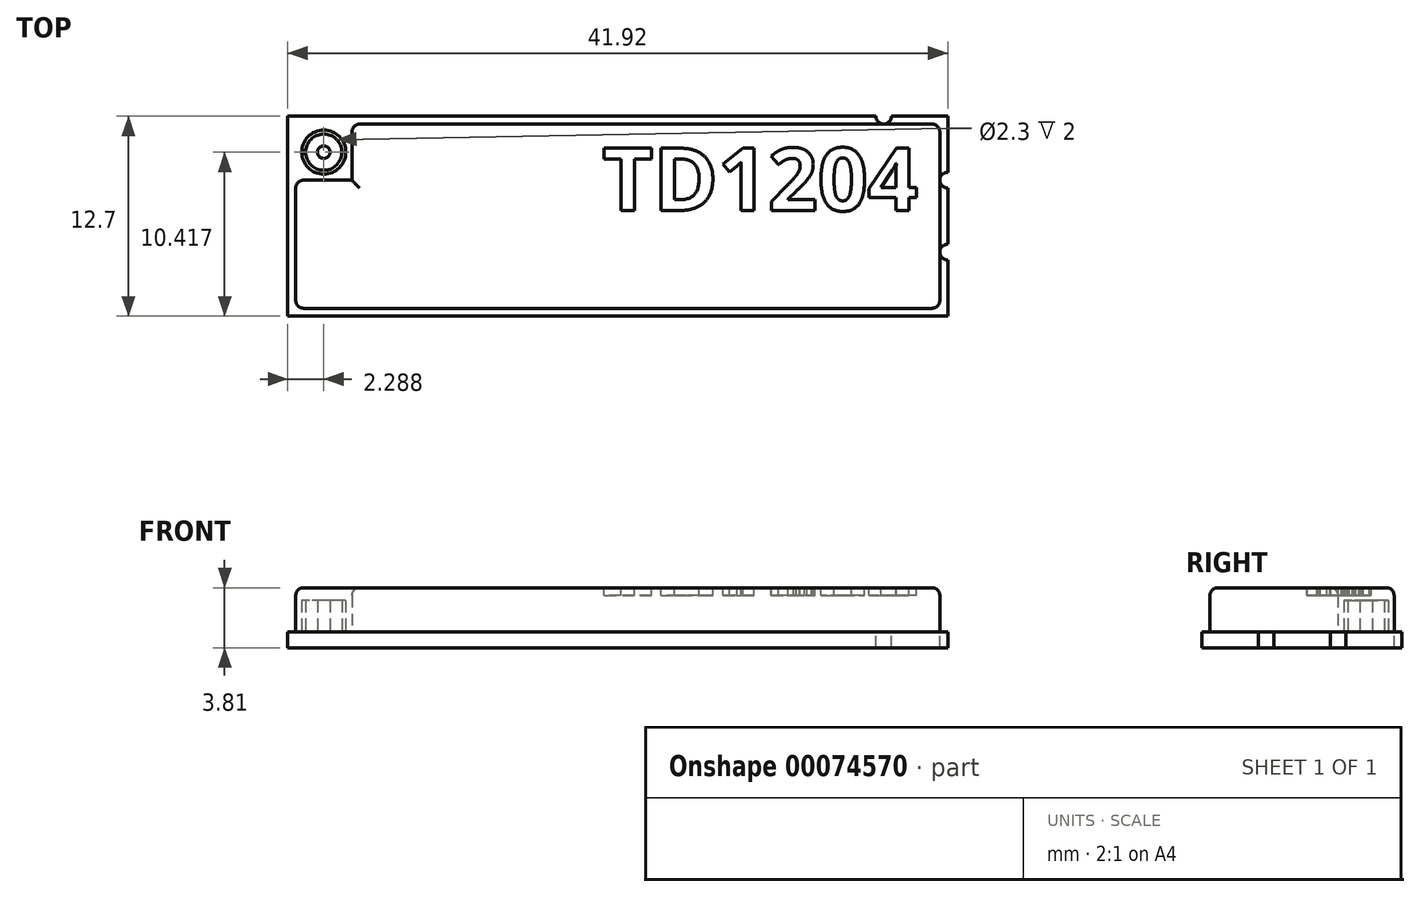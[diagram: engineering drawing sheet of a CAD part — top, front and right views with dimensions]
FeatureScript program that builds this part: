
annotation { "Feature Type Name" : "Feature", "Feature Type Description" : "" }
export const myFeature = defineFeature(function(context is Context, id is Id, definition is map)
    precondition{}
    {
        {
            var Q0;
            Q0=qCreatedBy(makeId("Top.planeOp"),FACE);
            var sketch = newSketch(context, id + "F0", { "sketchPlane" : qUnion([Q0])});
            skLineSegment(sketch, "E0.rect.bottom", {"start": v(-20.95, -6.35) * mm, "end": v(20.95, -6.35) * mm});
            skLineSegment(sketch, "E0.rect.top", {"start": v(-20.95, 6.35) * mm, "end": v(16.39, 6.35) * mm});
            skLineSegment(sketch, "E0.rect.left", {"start": v(-20.95, -6.35) * mm, "end": v(-20.95, 6.35) * mm});
            skLineSegment(sketch, "E0.rect.right", {"start": v(20.95, -6.35) * mm, "end": v(20.95, -2.78) * mm});
            skPoint(sketch, "E0.rect.middle", {"position": v(0, 0) * mm});
            skLineSegment(sketch, "E1.0", {"start": v(-16.89, 5.85) * mm, "end": v(20.45, 5.85) * mm});
            skLineSegment(sketch, "E1.1", {"start": v(-20.45, -5.85) * mm, "end": v(-20.45, 2.28) * mm});
            skLineSegment(sketch, "E1.2", {"start": v(-20.45, -5.85) * mm, "end": v(20.45, -5.85) * mm});
            skLineSegment(sketch, "E1.3", {"start": v(20.45, -5.85) * mm, "end": v(20.45, 5.85) * mm});
            skArc(sketch, "E2", {"start": v(20.95, 2.78) * mm, "mid": v(20.45, 2.28) * mm, "end": v(20.95, 1.78) * mm});
            skArc(sketch, "E3", {"start": v(20.95, -1.78) * mm, "mid": v(20.45, -2.28) * mm, "end": v(20.95, -2.78) * mm});
            skLineSegment(sketch, "E4.trimOffspring", {"start": v(20.95, 2.78) * mm, "end": v(20.95, 6.35) * mm});
            skLineSegment(sketch, "E5.trimOffspring", {"start": v(20.95, -1.78) * mm, "end": v(20.95, 1.78) * mm});
            skLineSegment(sketch, "E6", {"start": v(20.45, 5.85) * mm, "end": v(20.95, 6.35) * mm, "construction": true});
            skArc(sketch, "E7.MirrorCS", {"start": v(17.39, 6.35) * mm, "mid": v(16.89, 5.85) * mm, "end": v(16.39, 6.35) * mm});
            skLineSegment(sketch, "E8.trimOffspring", {"start": v(17.39, 6.35) * mm, "end": v(20.95, 6.35) * mm});
            skLineSegment(sketch, "E9", {"start": v(-20.45, 2.28) * mm, "end": v(-16.89, 2.28) * mm});
            skLineSegment(sketch, "E10", {"start": v(-16.89, 2.28) * mm, "end": v(-16.89, 5.85) * mm});
            skLineSegment(sketch, "E11", {"start": v(-20.45, 2.28) * mm, "end": v(-16.89, 5.85) * mm, "construction": true});
            skCircle(sketch, "E12", {"center": v(-18.67, 4.07) * mm, "radius": 1.4 * mm});
            skCircle(sketch, "E13", {"center": v(-18.67, 4.07) * mm, "radius": 1.15 * mm});
            skCircle(sketch, "E14", {"center": v(-18.67, 4.07) * mm, "radius": 0.4 * mm});
            skSolve(sketch);
        }
        {
            var Q0;
            Q0=makeQuery(id+"F0.imprint","IMPRINT",FACE,{"disambiguationData":[TD([[makeQuery(id+"F0.imprint","IMPRINT",EDGE,{"derivedFrom":sQuery(id+"F0.wireOp",EDGE,"E1.1")}),-1.0]])]});
            extrude(context, id + "F1", {"entities" : qUnion([Q0]), "depth" : (3.81 - 1) * mm});
        }
        {
            var Q0;
            Q0=makeQuery(id+"F0.imprint","IMPRINT",FACE,{"disambiguationData":[TD([[makeQuery(id+"F0.imprint","IMPRINT",EDGE,{"derivedFrom":sQuery(id+"F0.wireOp",EDGE,"E0.rect.bottom")}),1.0]])]});
            var Q1;
            Q1=makeQuery(id+"F0.imprint","IMPRINT",FACE,{"disambiguationData":[TD([[makeQuery(id+"F0.imprint","IMPRINT",EDGE,{"derivedFrom":sQuery(id+"F0.wireOp",EDGE,"E12")}),1.0]])]});
            var Q2;
            Q2=makeQuery(id+"F0.imprint","IMPRINT",FACE,{"disambiguationData":[TD([[makeQuery(id+"F0.imprint","IMPRINT",EDGE,{"derivedFrom":sQuery(id+"F0.wireOp",EDGE,"E13")}),1.0]])]});
            var Q3;
            {var subQ5=sQuery(id+"F0.wireOp",EDGE,"E5.trimOffspring");Q3=makeQuery(id+"F0.imprint","IMPRINT",FACE,{"disambiguationData":[TD([[makeQuery(id+"F0.imprint","IMPRINT",EDGE,{"derivedFrom":subQ5}),1.0]])]});}
            var Q4;
            {var subQ0=sQuery(id+"F0.wireOp",EDGE,"E4.trimOffspring");Q4=makeQuery(id+"F0.imprint","IMPRINT",FACE,{"disambiguationData":[TD([[makeQuery(id+"F0.imprint","IMPRINT",EDGE,{"derivedFrom":subQ0}),1.0]])]});}
            var Q5;
            Q5=makeQuery(id+"F0.imprint","IMPRINT",FACE,{"disambiguationData":[TD([[makeQuery(id+"F0.imprint","IMPRINT",EDGE,{"derivedFrom":sQuery(id+"F0.wireOp",EDGE,"E1.1")}),-1.0]])]});
            var Q6;
            Q6=makeQuery(id+"F0.imprint","IMPRINT",FACE,{"disambiguationData":[TD([[makeQuery(id+"F0.imprint","IMPRINT",EDGE,{"derivedFrom":sQuery(id+"F0.wireOp",EDGE,"E14")}),1.0]])]});
            extrude(context, id + "F2", {"entities" : qUnion([Q0, Q1, Q2, Q3, Q4, Q5, Q6]), "operationType" : NewBodyOperationType.ADD, "oppositeDirection" : true, "depth" : 1 * mm});
        }
        {
            var Q0;
            Q0=makeQuery(id+"F0.imprint","IMPRINT",FACE,{"disambiguationData":[TD([[makeQuery(id+"F0.imprint","IMPRINT",EDGE,{"derivedFrom":sQuery(id+"F0.wireOp",EDGE,"E12")}),1.0]])]});
            var Q1;
            Q1=makeQuery(id+"F0.imprint","IMPRINT",FACE,{"disambiguationData":[TD([[makeQuery(id+"F0.imprint","IMPRINT",EDGE,{"derivedFrom":sQuery(id+"F0.wireOp",EDGE,"E14")}),1.0]])]});
            extrude(context, id + "F3", {"entities" : qUnion([Q0, Q1]), "operationType" : NewBodyOperationType.ADD, "depth" : 2 * mm});
        }
        {
            var Q0;
            Q0=makeQuery(id+"F1.opExtrude","CAP_FACE",FACE,{"disambiguationData":[OSD([sQuery(id+"F0.wireOp",EDGE,"E1.0"),sQuery(id+"F0.wireOp",EDGE,"E1.1"),sQuery(id+"F0.wireOp",EDGE,"E1.2"),sQuery(id+"F0.wireOp",EDGE,"E1.3"),sQuery(id+"F0.wireOp",EDGE,"E9"),sQuery(id+"F0.wireOp",EDGE,"E10")])],"isStart":false});
            var Q1;
            Q1=makeQuery(id+"F1.opExtrude","SWEPT_EDGE",EDGE,{"disambiguationData":[OSD([sQuery(id+"F0.wireOp",EDGE,"E1.0"),sQuery(id+"F0.wireOp",EDGE,"E10")])]});
            var Q2;
            Q2=makeQuery(id+"F1.opExtrude","SWEPT_EDGE",EDGE,{"disambiguationData":[OSD([sQuery(id+"F0.wireOp",EDGE,"E1.1"),sQuery(id+"F0.wireOp",EDGE,"E9")])]});
            var Q3;
            Q3=makeQuery(id+"F1.opExtrude","SWEPT_EDGE",EDGE,{"disambiguationData":[OSD([sQuery(id+"F0.wireOp",EDGE,"E1.1"),sQuery(id+"F0.wireOp",EDGE,"E1.2")])]});
            var Q4;
            Q4=makeQuery(id+"F1.opExtrude","SWEPT_EDGE",EDGE,{"disambiguationData":[OSD([sQuery(id+"F0.wireOp",EDGE,"E1.0"),sQuery(id+"F0.wireOp",EDGE,"E1.3")])]});
            var Q5;
            Q5=makeQuery(id+"F1.opExtrude","SWEPT_EDGE",EDGE,{"disambiguationData":[OSD([sQuery(id+"F0.wireOp",EDGE,"E1.2"),sQuery(id+"F0.wireOp",EDGE,"E1.3")])]});
            fillet(context, id + "F4", {"entities" : qUnion([Q0, Q1, Q2, Q3, Q4, Q5]), "radius" : 0.5 * mm, "tangentPropagation" : true, "allowEdgeOverflow" : false});
        }
        {
            var Q0;
            Q0=makeQuery(id+"F1.opExtrude","CAP_FACE",FACE,{"disambiguationData":[OSD([sQuery(id+"F0.wireOp",EDGE,"E1.0"),sQuery(id+"F0.wireOp",EDGE,"E1.1"),sQuery(id+"F0.wireOp",EDGE,"E1.2"),sQuery(id+"F0.wireOp",EDGE,"E1.3"),sQuery(id+"F0.wireOp",EDGE,"E9"),sQuery(id+"F0.wireOp",EDGE,"E10")])],"isStart":false});
            var sketch = newSketch(context, id + "F5", { "sketchPlane" : qUnion([Q0])});
            skText(sketch, "E15", { "text": "TD1204", "fontName": "OpenSans-Bold.ttf"});
            const initialGuessF5  = {"E15": [-0.00097, 0.00035, 1, 0, 0.004]};
            skSetInitialGuess(sketch, initialGuessF5);
            skSolve(sketch);
        }
        {
            var Q0;
            Q0 = qSketchRegion(id + "F5", true);
            extrude(context, id + "F6", {"entities" : qUnion([Q0]), "operationType" : NewBodyOperationType.REMOVE, "oppositeDirection" : true, "depth" : 0.5 * mm});
        }
    });
